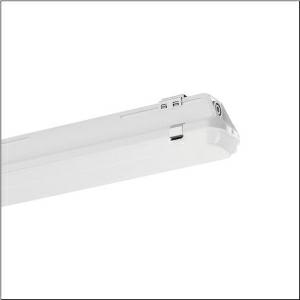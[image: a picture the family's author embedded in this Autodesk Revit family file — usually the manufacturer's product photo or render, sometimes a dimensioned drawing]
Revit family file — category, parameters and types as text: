
# Revit family: monsun_r__21_parking_51fg20dl430k_fea0
name_source: partatom
category: Lighting Fixtures
units: mm (PartAtom-declared; Revit-internal decimal feet)

## family parameters
Cut with Voids When Loaded = No
Host = Face
Light Source = No
Part Type = Normal
Room Calculation Point = No
Round Connector Dimension = Use Diameter
Shared = No

## types (1)
- --- (1 x LED, 3850 lm, 24 W, 4000K)
    Apparent Load = 24 VA
    CIE Flux Codes = 45 75 93 94 100
    Color Rendering = 80
    Color Temperature = 4000K
    Default Elevation = 1800 mm
    Description = Monsun® 21 parking, damp-proof luminaire, chain hanger, primary optical cover: enclosure, of PC, light emission: direct distribution, primary light characteristic: symmetric, installation type: suspended mounting, surface-mounted, horizontal mounting, vertical mounting, LED, rated luminous flux: 3.850lm, luminous efficacy: 160lm/W, light colour: 840, colour temperature: 4000K, control gear: DALI 2, with terminal, 5-pole, max. 2.5mm², mains connection: 220..240V, AC, 50/60Hz, rated input power: 24W, housing, of glass-fibre reinforced plastic, uncoated, bright grey, incl. chain hanger, length: 1.299mm, width: 90mm, height: 88mm, clip for enclosure, of stainless steel (V2A), ceiling mounting element, of stainless steel (V2A), chain hanger, of stainless steel (V2A), protection rating (complete): IP66, insulation class (complete): insulation class I (protective earthing), certification: CE, ENEC, VDE, UKCA, protection symbol: D, impact resistance: IK08, permissible operating ambient temperature: -25..+35°C, standard: EN 50419, EN 60598-2-1, corresponds to IFS (International Featured Standards) requirements for safety and quality in the food industry, for indoor or canopied outdoor use, no direct snow, no direct sun, no direct rain, LABS conformity tested according to VDMA 24364:2018-05, contact your sales advisor before using the luminaires in applications with unclear chemical exposure, large temperature fluctuations or condensation-forming humidity, packaging unit: 1 piece
    Height = 88 mm
    Lamp = 1 x LED
    Lamp Light Flux = 3850 lm
    Lamp Power = 24 W
    Lamp count = 1
    Length = 1299 mm
    Luminous efficacy = 160 lm/W
    Manufacturer = Siteco
    ModVariant = No
    Model = 51FG20DL430K
    Mounting Place = Ceiling
    Mounting Type = Surface mounted
    Number of Poles = 1
    OnlyDefault = Yes
    Power Factor = 1
    Product Name = Monsun® 21 parking
    Product group = damp-proof luminaire
    ProductGroupID = 301
    Protection Class = Protection class I
    Protection Degree = IP 66
    RLX_Detail_Level = 1
    RLX_Emergency_Light_Flux = 0 lm
    RLX_Emergency_Type = 0
    RLX_Emergency_Type_DB = No
    RlxData = <blob elided: 93673 chars, md5=d02b1ac6>
    Socket = socket
    Standby Power = 0 W
    System Light Flux = 3850 lm
    System Power = 24 W
    Type Comments = factory setting: luminous flux: 100 % | dim-lin: 254 | 161 mA
    Type Image = l_1319656.jpg
    URL = http://relux.com
    VarID = @adj_042405
    Voltage = 0 V
    Weight = 0.00 kg
    Width = 90 mm

## geometry (parser evidence)
native form markers: Blend x4, Sweep x14
no freeform markers — native parametric forms only
